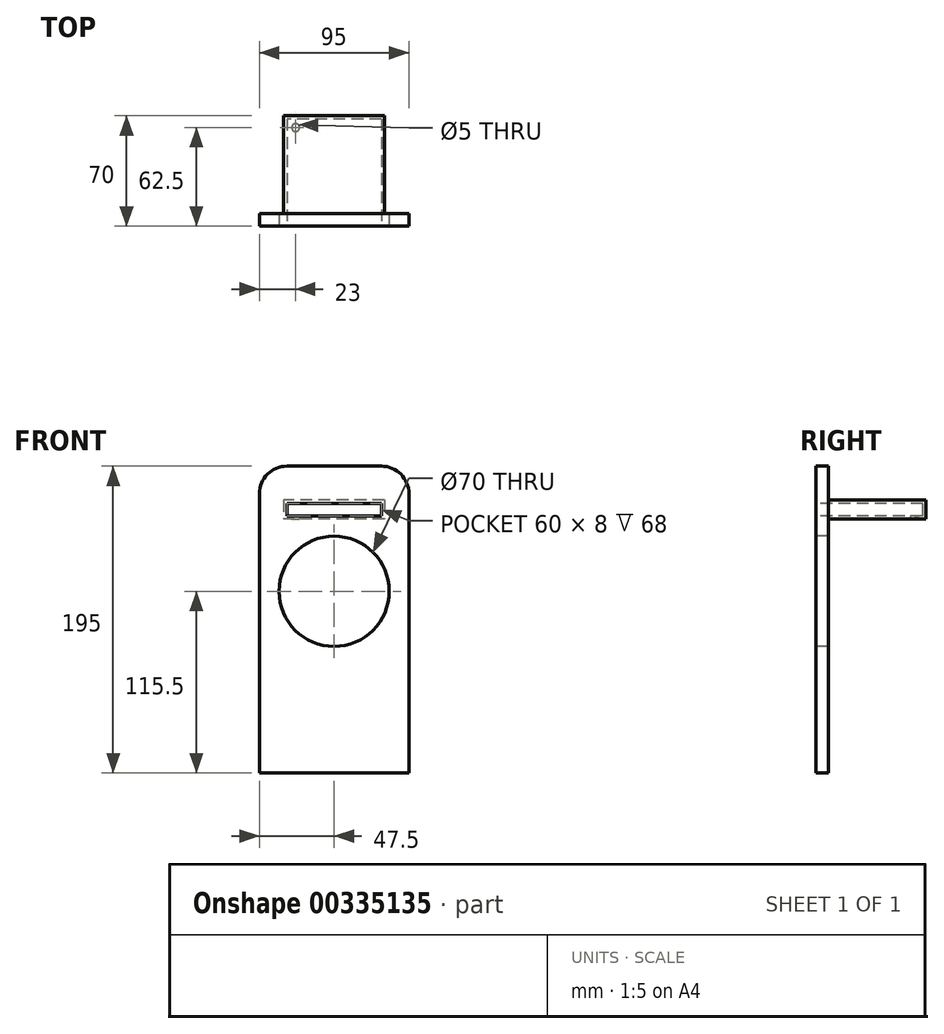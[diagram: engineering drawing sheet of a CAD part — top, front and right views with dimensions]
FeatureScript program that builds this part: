
annotation { "Feature Type Name" : "Feature", "Feature Type Description" : "" }
export const myFeature = defineFeature(function(context is Context, id is Id, definition is map)
    precondition{}
    {
        {
            var Q0;
            Q0=qCreatedBy(makeId("Front.planeOp"),FACE);
            var sketch = newSketch(context, id + "F0", { "sketchPlane" : qUnion([Q0])});
            skLineSegment(sketch, "E0.bottom", {"start": v(-30, 44.5) * mm, "end": v(30, 44.5) * mm});
            skLineSegment(sketch, "E0.top", {"start": v(-47.5, -150.5) * mm, "end": v(47.5, -150.5) * mm});
            skLineSegment(sketch, "E0.left", {"start": v(-47.5, 27) * mm, "end": v(-47.5, -150.5) * mm});
            skLineSegment(sketch, "E0.right", {"start": v(47.5, 27) * mm, "end": v(47.5, -150.5) * mm});
            skPoint(sketch, "E1.visualSharp", {"position": v(-47.5, 44.5) * mm});
            skArc(sketch, "E1.filletArc", {"start": v(-30, 44.5) * mm, "mid": v(-42.37, 39.38) * mm, "end": v(-47.5, 27) * mm});
            skPoint(sketch, "E2.visualSharp", {"position": v(47.5, 44.5) * mm});
            skArc(sketch, "E2.filletArc", {"start": v(47.5, 27) * mm, "mid": v(42.37, 39.38) * mm, "end": v(30, 44.5) * mm});
            skSolve(sketch);
        }
        {
            var Q0;
            Q0=makeQuery(id+"F0.imprint","IMPRINT",FACE,{"disambiguationData":[TD([[makeQuery(id+"F0.imprint","IMPRINT",EDGE,{"derivedFrom":sQuery(id+"F0.wireOp",EDGE,"E0.bottom")}),-1.0]])]});
            extrude(context, id + "F1", {"entities" : qUnion([Q0]), "depth" : 8 * mm});
        }
        {
            var Q0;
            Q0=makeQuery(id+"F1.opExtrude","CAP_FACE",FACE,{"disambiguationData":[OSD([sQuery(id+"F0.wireOp",EDGE,"E0.bottom"),sQuery(id+"F0.wireOp",EDGE,"E0.top"),sQuery(id+"F0.wireOp",EDGE,"E0.left"),sQuery(id+"F0.wireOp",EDGE,"E0.right"),sQuery(id+"F0.wireOp",EDGE,"E1.filletArc"),sQuery(id+"F0.wireOp",EDGE,"E2.filletArc")])],"isStart":false});
            var sketch = newSketch(context, id + "F2", { "sketchPlane" : qUnion([Q0])});
            skCircle(sketch, "E3", {"center": v(0, -35) * mm, "radius": 35 * mm});
            skSolve(sketch);
        }
        {
            var Q0;
            Q0=makeQuery(id+"F2.imprint","IMPRINT",FACE,{"disambiguationData":[TD([[makeQuery(id+"F2.imprint","IMPRINT",EDGE,{"derivedFrom":sQuery(id+"F2.wireOp",EDGE,"E3")}),1.0]])]});
            extrude(context, id + "F3", {"entities" : qUnion([Q0]), "operationType" : NewBodyOperationType.REMOVE, "oppositeDirection" : true, "depth" : 10 * mm});
        }
        {
            var Q0;
            Q0=makeQuery(id+"F1.opExtrude","CAP_FACE",FACE,{"disambiguationData":[OSD([sQuery(id+"F0.wireOp",EDGE,"E0.bottom"),sQuery(id+"F0.wireOp",EDGE,"E0.top"),sQuery(id+"F0.wireOp",EDGE,"E0.left"),sQuery(id+"F0.wireOp",EDGE,"E0.right"),sQuery(id+"F0.wireOp",EDGE,"E1.filletArc"),sQuery(id+"F0.wireOp",EDGE,"E2.filletArc")])],"isStart":false});
            var sketch = newSketch(context, id + "F4", { "sketchPlane" : qUnion([Q0])});
            skLineSegment(sketch, "E4.bottom", {"start": v(0, 12.86) * mm, "end": v(-30, 12.86) * mm});
            skLineSegment(sketch, "E4.top", {"start": v(0, 20.86) * mm, "end": v(-30, 20.86) * mm});
            skLineSegment(sketch, "E4.left", {"start": v(0, 12.86) * mm, "end": v(0, 20.86) * mm});
            skLineSegment(sketch, "E4.right", {"start": v(-30, 12.86) * mm, "end": v(-30, 20.86) * mm});
            skLineSegment(sketch, "E5.bottom", {"start": v(0, 12.86) * mm, "end": v(30, 12.86) * mm});
            skLineSegment(sketch, "E5.top", {"start": v(0, 20.86) * mm, "end": v(30, 20.86) * mm});
            skLineSegment(sketch, "E5.right", {"start": v(30, 12.86) * mm, "end": v(30, 20.86) * mm});
            skSolve(sketch);
        }
        {
            var Q0;
            Q0=makeQuery(id+"F4.imprint","IMPRINT",FACE,{"disambiguationData":[TD([[makeQuery(id+"F4.imprint","IMPRINT",EDGE,{"derivedFrom":sQuery(id+"F4.wireOp",EDGE,"E4.bottom")}),-1.0]])]});
            var Q1;
            Q1=makeQuery(id+"F4.imprint","IMPRINT",FACE,{"disambiguationData":[TD([[makeQuery(id+"F4.imprint","IMPRINT",EDGE,{"derivedFrom":sQuery(id+"F4.wireOp",EDGE,"E5.bottom")}),1.0]])]});
            extrude(context, id + "F5", {"entities" : qUnion([Q0, Q1]), "operationType" : NewBodyOperationType.REMOVE, "oppositeDirection" : true, "depth" : 8 * mm});
        }
        {
            var Q0;
            Q0=makeQuery(id+"F1.opExtrude","CAP_FACE",FACE,{"disambiguationData":[OSD([sQuery(id+"F0.wireOp",EDGE,"E0.bottom"),sQuery(id+"F0.wireOp",EDGE,"E0.top"),sQuery(id+"F0.wireOp",EDGE,"E0.left"),sQuery(id+"F0.wireOp",EDGE,"E0.right"),sQuery(id+"F0.wireOp",EDGE,"E1.filletArc"),sQuery(id+"F0.wireOp",EDGE,"E2.filletArc")])],"isStart":true});
            var sketch = newSketch(context, id + "F6", { "sketchPlane" : qUnion([Q0])});
            skLineSegment(sketch, "E6.bottom", {"start": v(-30, 20.86) * mm, "end": v(30, 20.86) * mm});
            skLineSegment(sketch, "E6.top", {"start": v(-30, 22.86) * mm, "end": v(30, 22.86) * mm});
            skLineSegment(sketch, "E6.left", {"start": v(-30, 20.86) * mm, "end": v(-30, 22.86) * mm});
            skLineSegment(sketch, "E6.right", {"start": v(30, 20.86) * mm, "end": v(30, 22.86) * mm});
            skLineSegment(sketch, "E7.bottom", {"start": v(30, 22.86) * mm, "end": v(32, 22.86) * mm});
            skLineSegment(sketch, "E7.top", {"start": v(30, 10.86) * mm, "end": v(32, 10.86) * mm});
            skLineSegment(sketch, "E7.left", {"start": v(30, 22.86) * mm, "end": v(30, 10.86) * mm});
            skLineSegment(sketch, "E7.right", {"start": v(32, 22.86) * mm, "end": v(32, 10.86) * mm});
            skLineSegment(sketch, "E8.bottom", {"start": v(-30, 12.86) * mm, "end": v(30, 12.86) * mm});
            skLineSegment(sketch, "E8.top", {"start": v(-30, 10.86) * mm, "end": v(30, 10.86) * mm});
            skLineSegment(sketch, "E8.left", {"start": v(-30, 12.86) * mm, "end": v(-30, 10.86) * mm});
            skLineSegment(sketch, "E8.right", {"start": v(30, 12.86) * mm, "end": v(30, 10.86) * mm});
            skLineSegment(sketch, "E9.bottom", {"start": v(-30, 22.86) * mm, "end": v(-32, 22.86) * mm});
            skLineSegment(sketch, "E9.top", {"start": v(-30, 10.86) * mm, "end": v(-32, 10.86) * mm});
            skLineSegment(sketch, "E9.left", {"start": v(-30, 22.86) * mm, "end": v(-30, 10.86) * mm});
            skLineSegment(sketch, "E9.right", {"start": v(-32, 22.86) * mm, "end": v(-32, 10.86) * mm});
            skSolve(sketch);
        }
        {
            var Q0;
            {var subQ3=sQuery(id+"F6.wireOp",EDGE,"E7.bottom");Q0=makeQuery(id+"F6.imprint","IMPRINT",FACE,{"disambiguationData":[TD([[makeQuery(id+"F6.imprint","IMPRINT",EDGE,{"derivedFrom":subQ3}),-1.0]])]});}
            var Q1;
            {var subQ0=sQuery(id+"F6.wireOp",EDGE,"E8.bottom");Q1=makeQuery(id+"F6.imprint","IMPRINT",FACE,{"disambiguationData":[TD([[makeQuery(id+"F6.imprint","IMPRINT",EDGE,{"derivedFrom":subQ0}),-1.0]])]});}
            var Q2;
            {var subQ3=sQuery(id+"F6.wireOp",EDGE,"E9.bottom");Q2=makeQuery(id+"F6.imprint","IMPRINT",FACE,{"disambiguationData":[TD([[makeQuery(id+"F6.imprint","IMPRINT",EDGE,{"derivedFrom":subQ3}),1.0]])]});}
            var Q3;
            {var subQ0=sQuery(id+"F6.wireOp",EDGE,"E6.bottom");Q3=makeQuery(id+"F6.imprint","IMPRINT",FACE,{"disambiguationData":[TD([[makeQuery(id+"F6.imprint","IMPRINT",EDGE,{"derivedFrom":subQ0}),1.0]])]});}
            extrude(context, id + "F7", {"entities" : qUnion([Q0, Q1, Q2, Q3]), "operationType" : NewBodyOperationType.ADD, "depth" : 60 * mm});
        }
        {
            var Q0;
            Q0=makeQuery(id+"F7.opExtrude","CAP_FACE",FACE,{"disambiguationData":[OSD([sQuery(id+"F6.wireOp",EDGE,"E6.bottom"),sQuery(id+"F6.wireOp",EDGE,"E6.top"),sQuery(id+"F6.wireOp",EDGE,"E7.bottom"),sQuery(id+"F6.wireOp",EDGE,"E7.top"),sQuery(id+"F6.wireOp",EDGE,"E7.left"),sQuery(id+"F6.wireOp",EDGE,"E7.right"),sQuery(id+"F6.wireOp",EDGE,"E8.bottom"),sQuery(id+"F6.wireOp",EDGE,"E8.top"),sQuery(id+"F6.wireOp",EDGE,"E9.bottom"),sQuery(id+"F6.wireOp",EDGE,"E9.top"),sQuery(id+"F6.wireOp",EDGE,"E9.left"),sQuery(id+"F6.wireOp",EDGE,"E9.right")])],"isStart":false});
            var sketch = newSketch(context, id + "F8", { "sketchPlane" : qUnion([Q0])});
            skLineSegment(sketch, "E10.bottom", {"start": v(-32, 22.86) * mm, "end": v(32, 22.86) * mm});
            skLineSegment(sketch, "E10.top", {"start": v(-32, 10.86) * mm, "end": v(32, 10.86) * mm});
            skLineSegment(sketch, "E10.left", {"start": v(-32, 22.86) * mm, "end": v(-32, 10.86) * mm});
            skLineSegment(sketch, "E10.right", {"start": v(32, 22.86) * mm, "end": v(32, 10.86) * mm});
            skSolve(sketch);
        }
        {
            var Q0;
            Q0 = qSketchRegion(id + "F8", true);
            extrude(context, id + "F9", {"entities" : qUnion([Q0]), "operationType" : NewBodyOperationType.ADD, "depth" : 2 * mm});
        }
        {
            var Q0;
            Q0=makeQuery(id+"F9.boolean.opBoolean","MERGE",FACE,{"derivedFrom":[makeQuery(id+"F7.opExtrude","SWEPT_FACE",FACE,{"disambiguationData":[OSD([sQuery(id+"F6.wireOp",EDGE,"E7.top"),sQuery(id+"F6.wireOp",EDGE,"E8.top"),sQuery(id+"F6.wireOp",EDGE,"E9.top")])]}),makeQuery(id+"F9.opExtrude","SWEPT_FACE",FACE,{"disambiguationData":[OSD([sQuery(id+"F8.wireOp",EDGE,"E10.top")])]})]});
            var sketch = newSketch(context, id + "F10", { "sketchPlane" : qUnion([Q0])});
            skCircle(sketch, "E11", {"center": v(-24.5, -54.5) * mm, "radius": 2.5 * mm});
            skSolve(sketch);
        }
        {
            var Q0;
            Q0=makeQuery(id+"F10.imprint","IMPRINT",FACE,{"disambiguationData":[TD([[makeQuery(id+"F10.imprint","IMPRINT",EDGE,{"derivedFrom":sQuery(id+"F10.wireOp",EDGE,"E11")}),1.0]])]});
            extrude(context, id + "F11", {"entities" : qUnion([Q0]), "operationType" : NewBodyOperationType.REMOVE, "oppositeDirection" : true, "depth" : 4 * mm});
        }
        {
            var Q0;
            Q0=qCreatedBy(makeId("Right.planeOp"),FACE);
            var sketch = newSketch(context, id + "F12", { "sketchPlane" : qUnion([Q0])});
            skLineSegment(sketch, "E12", {"start": v(0, 0) * mm, "end": v(50, -26.54) * mm});
            skLineSegment(sketch, "E13", {"start": v(50, -35) * mm, "end": v(0, -35) * mm});
            skLineSegment(sketch, "E14", {"start": v(0, 0) * mm, "end": v(0, -35) * mm});
            skLineSegment(sketch, "E15", {"start": v(50, -26.54) * mm, "end": v(50, -35) * mm});
            skSolve(sketch);
        }
        {
            var Q0;
            Q0=sQuery(id+"F12.wireOp",EDGE,"E12");
            var Q1;
            Q1=sQuery(id+"F12.wireOp",EDGE,"E13");
            revolve(context, id + "F13", {"bodyType" : ToolBodyType.SURFACE, "surfaceEntities" : qUnion([Q0]), "axis" : qUnion([Q1]), "revolveType" : RevolveType.FULL});
        }
    });
